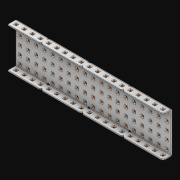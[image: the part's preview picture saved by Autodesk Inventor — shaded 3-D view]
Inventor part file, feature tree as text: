
AUTODESK INVENTOR PART (.ipt)
format: ipt  version: 2021 (Build 250183000, 183)  size: 3,339,264 bytes
history: native  units: in
note: dims shown in document units (in); Inventor stores cm internally (conversion verified against a paired STEP export)
features: extrude x134, other x133, sketch x4, thicken_offset x3, pattern_linear x3, imported_body x1
ambient origin geometry x8: Origin, YZ Plane, XZ Plane, XY Plane, X Axis, Y Axis, Z Axis, Center Point
bodies: Solid1 (feature_tree)
feature tree (278):
  thicken_offset  "Thicken1"
  thicken_offset  "Thicken2"
  thicken_offset  "Thicken3"
  pattern_linear  "Rectangular Pattern1"  Spacing1=0.001in  [1 undecoded]
  pattern_linear  "Rectangular Pattern2"  Spacing1=0.001in  [1 undecoded]
  pattern_linear  "Rectangular Pattern3"  Spacing1=0.182in  [1 undecoded]
  extrude  "Extrusion1"  Depth=0.063in TaperAngle=0.0deg
  sketch  "Sketch1"  dims[d0=0.001in]
  other  "Srf1"
  sketch  "Sketch2"  dims[d1=0.001in]
  other  "Srf2"
  sketch  "Sketch3"  dims[d2=0.001in]
  other  "Srf3"
  other  "Srf4"
  other  "Srf5"
  other  "Srf6"
  other  "Srf7"
  other  "Srf8"
  other  "Srf9"
  other  "Srf10"
  other  "Srf11"
  other  "Srf12"
  other  "Srf13"
  other  "Srf14"
  other  "Srf15"
  other  "Srf16"
  other  "Srf17"
  other  "Srf18"
  other  "Srf19"
  other  "Srf20"
  other  "Srf21"
  other  "Srf38"
  other  "Srf39"
  other  "Srf40"
  other  "Srf41"
  other  "Srf42"
  other  "Srf43"
  other  "Srf44"
  other  "Srf45"
  other  "Srf46"
  other  "Srf47"
  other  "Srf48"
  other  "Srf49"
  other  "Srf50"
  other  "Srf51"
  other  "Srf52"
  other  "Srf53"
  other  "Srf54"
  other  "Srf55"
  other  "Srf72"
  other  "Srf73"
  other  "Srf74"
  other  "Srf75"
  other  "Srf76"
  other  "Srf77"
  other  "Srf78"
  other  "Srf79"
  other  "Srf80"
  other  "Srf81"
  other  "Srf82"
  other  "Srf83"
  other  "Srf84"
  other  "Srf85"
  other  "Srf86"
  other  "Srf87"
  other  "Srf88"
  other  "Srf89"
  other  "Srf106"
  other  "Srf107"
  other  "Srf108"
  other  "Srf109"
  other  "Srf110"
  other  "Srf111"
  other  "Srf112"
  other  "Srf113"
  other  "Srf114"
  other  "Srf115"
  other  "Srf116"
  other  "Srf117"
  other  "Srf118"
  other  "Srf119"
  other  "Srf120"
  other  "Srf121"
  other  "Srf122"
  other  "Srf123"
  other  "Srf124"
  other  "Srf141"
  other  "Srf142"
  other  "Srf143"
  other  "Srf144"
  other  "Srf145"
  other  "Srf146"
  other  "Srf147"
  other  "Srf148"
  other  "Srf149"
  other  "Srf150"
  other  "Srf151"
  other  "Srf152"
  other  "Srf153"
  other  "Srf154"
  other  "Srf155"
  other  "Srf156"
  other  "Srf157"
  other  "Srf158"
  other  "Srf159"
  other  "Srf176"
  other  "Srf177"
  other  "Srf178"
  other  "Srf179"
  other  "Srf180"
  other  "Srf181"
  other  "Srf182"
  other  "Srf183"
  other  "Srf184"
  other  "Srf185"
  other  "Srf186"
  other  "Srf187"
  other  "Srf188"
  other  "Srf189"
  other  "Srf190"
  other  "Srf191"
  other  "Srf192"
  other  "Srf193"
  other  "Srf194"
  other  "Srf211"
  other  "Srf212"
  other  "Srf213"
  other  "Srf214"
  other  "Srf215"
  other  "Srf216"
  other  "Srf217"
  other  "Srf218"
  other  "Srf219"
  other  "Srf220"
  other  "Srf221"
  other  "Srf222"
  other  "Srf223"
  other  "Srf224"
  other  "Srf225"
  other  "Srf226"
  other  "Srf227"
  other  "Srf228"
  other  "Srf229"
  sketch  "Sketch4"  dims[d3=0.001in d4=0.001in d5=0.001in d6=0.182in d7=0.063in d8=0.0in d9=0.182in d10=0.063in d11=0.0in d12=0.182in d13=0.063in d14=0.0in d17=0.5in d18=7.4803in d20=0.5in d21=7.4803in d23=0.5in d24=1.9685in d26=0.5in d27=8.0in d28=0.0in]
  imported_body  "Imported1"
  extrude  "ExtrusionSrf1"  Depth=8.0in
  extrude  "ExtrusionSrf2"  Depth=0.063in TaperAngle=0.0deg
  extrude  "ExtrusionSrf3"  Depth=8.0in
  extrude  "ExtrusionSrf4"  Depth=0.063in TaperAngle=0.0deg
  extrude  "ExtrusionSrf5"  Depth=0.5in
  extrude  "ExtrusionSrf6"  Depth=8.0in
  extrude  "ExtrusionSrf7"  Depth=0.5in
  extrude  "ExtrusionSrf8"  Depth=8.0in
  extrude  "ExtrusionSrf9"  Depth=0.5in
  extrude  "ExtrusionSrf10"  Depth=0.5in
  extrude  "ExtrusionSrf11"  Depth=8.0in
  extrude  "ExtrusionSrf12"  TaperAngle=0.0deg  [1 undecoded]
  extrude  "ExtrusionSrf13"  [1 undecoded]
  extrude  "ExtrusionSrf14"  [1 undecoded]
  extrude  "ExtrusionSrf15"  [1 undecoded]
  extrude  "ExtrusionSrf16"  [1 undecoded]
  extrude  "ExtrusionSrf17"  [1 undecoded]
  extrude  "ExtrusionSrf18"  [1 undecoded]
  extrude  "ExtrusionSrf19"  [1 undecoded]
  extrude  "ExtrusionSrf20"  [1 undecoded]
  extrude  "ExtrusionSrf21"  [1 undecoded]
  extrude  "ExtrusionSrf38"  [1 undecoded]
  extrude  "ExtrusionSrf39"  [1 undecoded]
  extrude  "ExtrusionSrf40"  [1 undecoded]
  extrude  "ExtrusionSrf41"  [1 undecoded]
  extrude  "ExtrusionSrf42"  [1 undecoded]
  extrude  "ExtrusionSrf43"  [1 undecoded]
  extrude  "ExtrusionSrf44"  [1 undecoded]
  extrude  "ExtrusionSrf45"  [1 undecoded]
  extrude  "ExtrusionSrf46"  [1 undecoded]
  extrude  "ExtrusionSrf47"  [1 undecoded]
  extrude  "ExtrusionSrf48"  [1 undecoded]
  extrude  "ExtrusionSrf49"  [1 undecoded]
  extrude  "ExtrusionSrf50"  [1 undecoded]
  extrude  "ExtrusionSrf51"  [1 undecoded]
  extrude  "ExtrusionSrf52"  [1 undecoded]
  extrude  "ExtrusionSrf53"  [1 undecoded]
  extrude  "ExtrusionSrf54"  [1 undecoded]
  extrude  "ExtrusionSrf55"  [1 undecoded]
  extrude  "ExtrusionSrf72"  [1 undecoded]
  extrude  "ExtrusionSrf73"  [1 undecoded]
  extrude  "ExtrusionSrf74"  [1 undecoded]
  extrude  "ExtrusionSrf75"  [1 undecoded]
  extrude  "ExtrusionSrf76"  [1 undecoded]
  extrude  "ExtrusionSrf77"  [1 undecoded]
  extrude  "ExtrusionSrf78"  [1 undecoded]
  extrude  "ExtrusionSrf79"  [1 undecoded]
  extrude  "ExtrusionSrf80"  [1 undecoded]
  extrude  "ExtrusionSrf81"  [1 undecoded]
  extrude  "ExtrusionSrf82"  [1 undecoded]
  extrude  "ExtrusionSrf83"  [1 undecoded]
  extrude  "ExtrusionSrf84"  [1 undecoded]
  extrude  "ExtrusionSrf85"  [1 undecoded]
  extrude  "ExtrusionSrf86"  [1 undecoded]
  extrude  "ExtrusionSrf87"  [1 undecoded]
  extrude  "ExtrusionSrf88"  [1 undecoded]
  extrude  "ExtrusionSrf89"  [1 undecoded]
  extrude  "ExtrusionSrf106"  [1 undecoded]
  extrude  "ExtrusionSrf107"  [1 undecoded]
  extrude  "ExtrusionSrf108"  [1 undecoded]
  extrude  "ExtrusionSrf109"  [1 undecoded]
  extrude  "ExtrusionSrf110"  [1 undecoded]
  extrude  "ExtrusionSrf111"  [1 undecoded]
  extrude  "ExtrusionSrf112"  [1 undecoded]
  extrude  "ExtrusionSrf113"  [1 undecoded]
  extrude  "ExtrusionSrf114"  [1 undecoded]
  extrude  "ExtrusionSrf115"  [1 undecoded]
  extrude  "ExtrusionSrf116"  [1 undecoded]
  extrude  "ExtrusionSrf117"  [1 undecoded]
  extrude  "ExtrusionSrf118"  [1 undecoded]
  extrude  "ExtrusionSrf119"  [1 undecoded]
  extrude  "ExtrusionSrf120"  [1 undecoded]
  extrude  "ExtrusionSrf121"  [1 undecoded]
  extrude  "ExtrusionSrf122"  [1 undecoded]
  extrude  "ExtrusionSrf123"  [1 undecoded]
  extrude  "ExtrusionSrf124"  [1 undecoded]
  extrude  "ExtrusionSrf141"  [1 undecoded]
  extrude  "ExtrusionSrf142"  [1 undecoded]
  extrude  "ExtrusionSrf143"  [1 undecoded]
  extrude  "ExtrusionSrf144"  [1 undecoded]
  extrude  "ExtrusionSrf145"  [1 undecoded]
  extrude  "ExtrusionSrf146"  [1 undecoded]
  extrude  "ExtrusionSrf147"  [1 undecoded]
  extrude  "ExtrusionSrf148"  [1 undecoded]
  extrude  "ExtrusionSrf149"  [1 undecoded]
  extrude  "ExtrusionSrf150"  [1 undecoded]
  extrude  "ExtrusionSrf151"  [1 undecoded]
  extrude  "ExtrusionSrf152"  [1 undecoded]
  extrude  "ExtrusionSrf153"  [1 undecoded]
  extrude  "ExtrusionSrf154"  [1 undecoded]
  extrude  "ExtrusionSrf155"  [1 undecoded]
  extrude  "ExtrusionSrf156"  [1 undecoded]
  extrude  "ExtrusionSrf157"  [1 undecoded]
  extrude  "ExtrusionSrf158"  [1 undecoded]
  extrude  "ExtrusionSrf159"  [1 undecoded]
  extrude  "ExtrusionSrf176"  [1 undecoded]
  extrude  "ExtrusionSrf177"  [1 undecoded]
  extrude  "ExtrusionSrf178"  [1 undecoded]
  extrude  "ExtrusionSrf179"  [1 undecoded]
  extrude  "ExtrusionSrf180"  [1 undecoded]
  extrude  "ExtrusionSrf181"  [1 undecoded]
  extrude  "ExtrusionSrf182"  [1 undecoded]
  extrude  "ExtrusionSrf183"  [1 undecoded]
  extrude  "ExtrusionSrf184"  [1 undecoded]
  extrude  "ExtrusionSrf185"  [1 undecoded]
  extrude  "ExtrusionSrf186"  [1 undecoded]
  extrude  "ExtrusionSrf187"  [1 undecoded]
  extrude  "ExtrusionSrf188"  [1 undecoded]
  extrude  "ExtrusionSrf189"  [1 undecoded]
  extrude  "ExtrusionSrf190"  [1 undecoded]
  extrude  "ExtrusionSrf191"  [1 undecoded]
  extrude  "ExtrusionSrf192"  [1 undecoded]
  extrude  "ExtrusionSrf193"  [1 undecoded]
  extrude  "ExtrusionSrf194"  [1 undecoded]
  extrude  "ExtrusionSrf211"  [1 undecoded]
  extrude  "ExtrusionSrf212"  [1 undecoded]
  extrude  "ExtrusionSrf213"  [1 undecoded]
  extrude  "ExtrusionSrf214"  [1 undecoded]
  extrude  "ExtrusionSrf215"  [1 undecoded]
  extrude  "ExtrusionSrf216"  [1 undecoded]
  extrude  "ExtrusionSrf217"  [1 undecoded]
  extrude  "ExtrusionSrf218"  [1 undecoded]
  extrude  "ExtrusionSrf219"  [1 undecoded]
  extrude  "ExtrusionSrf220"  [1 undecoded]
  extrude  "ExtrusionSrf221"  [1 undecoded]
  extrude  "ExtrusionSrf222"  [1 undecoded]
  extrude  "ExtrusionSrf223"  [1 undecoded]
  extrude  "ExtrusionSrf224"  [1 undecoded]
  extrude  "ExtrusionSrf225"  [1 undecoded]
  extrude  "ExtrusionSrf226"  [1 undecoded]
  extrude  "ExtrusionSrf227"  [1 undecoded]
  extrude  "ExtrusionSrf228"  [1 undecoded]
  extrude  "ExtrusionSrf229"  [1 undecoded]
note: 125 required parameter values undecoded (feature->parameter linkage not recoverable at this tier; creation-order binding heuristic only, values carry confidence <= 0.55)
